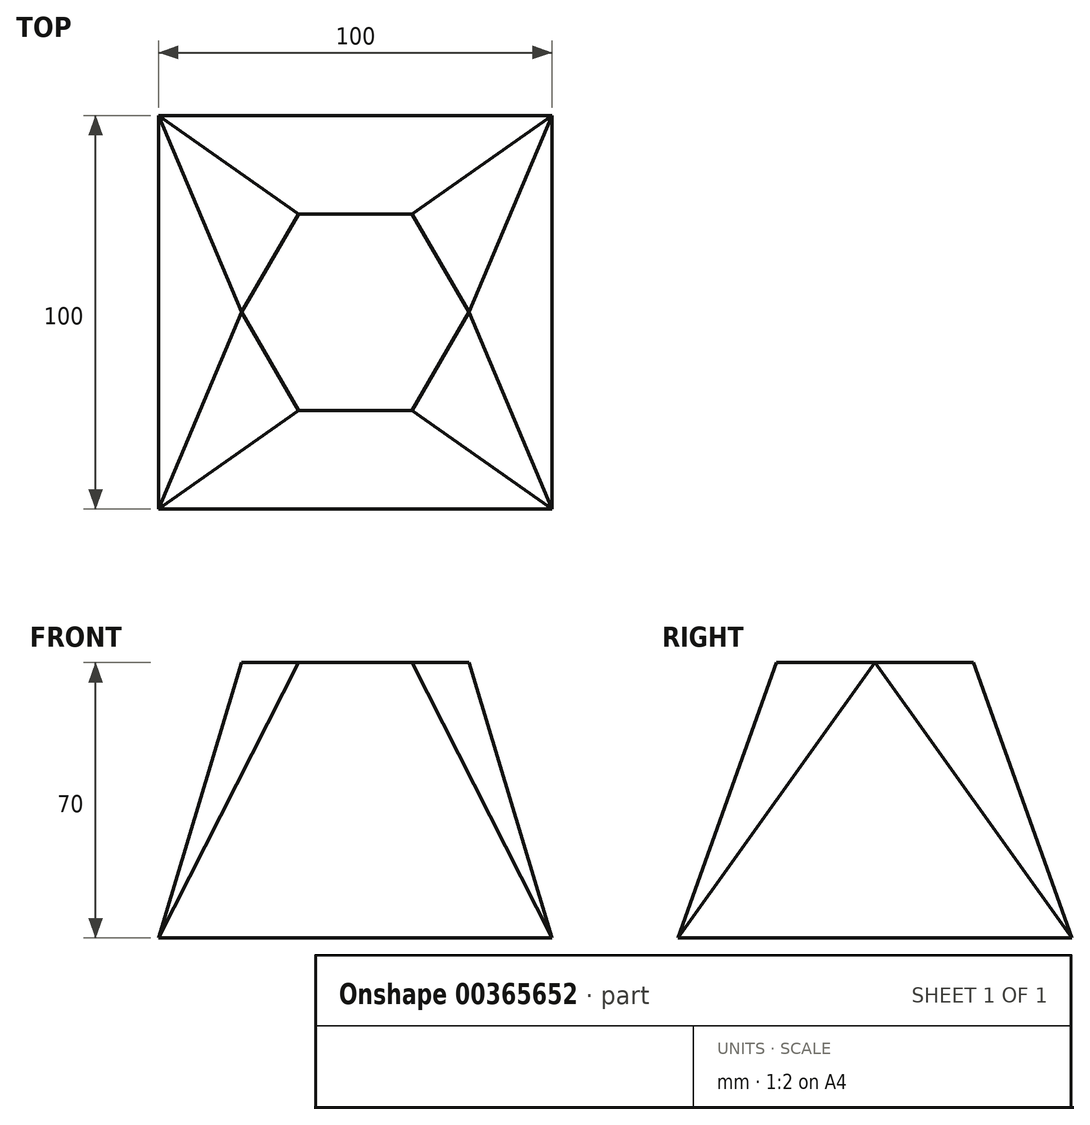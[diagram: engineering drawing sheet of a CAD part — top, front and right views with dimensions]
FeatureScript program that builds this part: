
annotation { "Feature Type Name" : "Feature", "Feature Type Description" : "" }
export const myFeature = defineFeature(function(context is Context, id is Id, definition is map)
    precondition{}
    {
        {
            var Q0;
            Q0=qCreatedBy(makeId("Top.planeOp"),FACE);
            cPlane(context, id + "F0", {"entities" : qUnion([Q0]), "cplaneType" : CPlaneType.OFFSET, "offset" : 70 * mm, "width" : 150 * mm, "height" : 150 * mm});
        }
        {
            var Q0;
            Q0=qCreatedBy(makeId("Top.planeOp"),FACE);
            var sketch = newSketch(context, id + "F1", { "sketchPlane" : qUnion([Q0])});
            skLineSegment(sketch, "E0.bottom", {"start": v(-50, -50) * mm, "end": v(50, -50) * mm});
            skLineSegment(sketch, "E0.top", {"start": v(-50, 50) * mm, "end": v(50, 50) * mm});
            skLineSegment(sketch, "E0.left", {"start": v(-50, -50) * mm, "end": v(-50, 50) * mm});
            skLineSegment(sketch, "E0.right", {"start": v(50, -50) * mm, "end": v(50, 50) * mm});
            skPoint(sketch, "E0.middle", {"position": v(0, 0) * mm});
            skSolve(sketch);
        }
        {
            var Q0;
            Q0=qCreatedBy(id+"F0.planeOp",FACE);
            var sketch = newSketch(context, id + "F2", { "sketchPlane" : qUnion([Q0])});
            skCircle(sketch, "E1.cCircle", {"center": v(0, 0) * mm, "radius": 25 * mm, "construction": true});
            skLineSegment(sketch, "E1.0", {"start": v(-14.43, 25) * mm, "end": v(14.43, 25) * mm});
            skLineSegment(sketch, "E1.1", {"start": v(14.43, 25) * mm, "end": v(28.87, 0) * mm});
            skLineSegment(sketch, "E1.2", {"start": v(28.87, 0) * mm, "end": v(14.43, -25) * mm});
            skLineSegment(sketch, "E1.3", {"start": v(14.43, -25) * mm, "end": v(-14.43, -25) * mm});
            skLineSegment(sketch, "E1.4", {"start": v(-14.43, -25) * mm, "end": v(-28.87, 0) * mm});
            skLineSegment(sketch, "E1.5", {"start": v(-28.87, 0) * mm, "end": v(-14.43, 25) * mm});
            skPoint(sketch, "E1.0.midPoint", {"position": v(0, 25) * mm});
            skLineSegment(sketch, "E2", {"start": v(14.43, 25) * mm, "end": v(28.87, 25) * mm});
            skLineSegment(sketch, "E3", {"start": v(28.87, 25) * mm, "end": v(28.87, 0) * mm});
            skLineSegment(sketch, "E4", {"start": v(28.87, 0) * mm, "end": v(28.87, -25) * mm});
            skLineSegment(sketch, "E5", {"start": v(28.87, -25) * mm, "end": v(14.43, -25) * mm});
            skLineSegment(sketch, "E6", {"start": v(-14.43, -25) * mm, "end": v(-28.87, -25) * mm});
            skLineSegment(sketch, "E7", {"start": v(-28.87, -25) * mm, "end": v(-28.87, 0) * mm});
            skLineSegment(sketch, "E8", {"start": v(-14.43, 25) * mm, "end": v(-28.87, 25) * mm});
            skLineSegment(sketch, "E9", {"start": v(-28.87, 25) * mm, "end": v(-28.87, 0) * mm});
            skSolve(sketch);
        }
        {
            var Q0;
            Q0=qCreatedBy(id+"F0.planeOp",FACE);
            var sketch = newSketch(context, id + "F3", { "sketchPlane" : qUnion([Q0])});
            skLineSegment(sketch, "E10.bottom", {"start": v(28.87, 25) * mm, "end": v(-28.87, 25) * mm});
            skLineSegment(sketch, "E10.top", {"start": v(28.87, -25) * mm, "end": v(-28.87, -25) * mm});
            skLineSegment(sketch, "E10.left", {"start": v(28.87, 25) * mm, "end": v(28.87, -25) * mm});
            skLineSegment(sketch, "E10.right", {"start": v(-28.87, 25) * mm, "end": v(-28.87, -25) * mm});
            skPoint(sketch, "E10.middle", {"position": v(0, 0) * mm});
            skSolve(sketch);
        }
        {
            var Q0;
            Q0=makeQuery(id+"F1.imprint","IMPRINT",FACE,{"disambiguationData":[TD([[makeQuery(id+"F1.imprint","IMPRINT",EDGE,{"derivedFrom":sQuery(id+"F1.wireOp",EDGE,"E0.bottom")}),1.0]])]});
            var Q1;
            Q1 = qSketchRegion(id + "F3", true);
            loft(context, id + "F4", {"sheetProfilesArray" : [{ "sheetProfileEntities" : qUnion([Q0]) }, { "sheetProfileEntities" : qUnion([Q1]) }]});
        }
        {
            var Q1;
            Q1=makeQuery(id+"F2.imprint","IMPRINT",FACE,{"disambiguationData":[TD([[makeQuery(id+"F2.imprint","IMPRINT",EDGE,{"derivedFrom":sQuery(id+"F2.wireOp",EDGE,"E1.5")}),1.0]])]});
            var Q2;
            Q2=makeQuery(id+"F4.opLoft","MID_CAP_VERTEX",VERTEX,{"disambiguationData":[OSD([sQuery(id+"F1.wireOp",EDGE,"E0.top"),sQuery(id+"F1.wireOp",EDGE,"E0.left")])],"capPos":0.0});
            loft(context, id + "F5", {"operationType" : NewBodyOperationType.REMOVE, "sheetProfilesArray" : [{ "sheetProfileEntities" : qUnion([Q1]) }, { "sheetProfileEntities" : qUnion([Q2]) }]});
        }
        {
            var Q1;
            Q1=makeQuery(id+"F2.imprint","IMPRINT",FACE,{"disambiguationData":[TD([[makeQuery(id+"F2.imprint","IMPRINT",EDGE,{"derivedFrom":sQuery(id+"F2.wireOp",EDGE,"E1.4")}),1.0]])]});
            var Q2;
            Q2=makeQuery(id+"F4.opLoft","MID_CAP_VERTEX",VERTEX,{"disambiguationData":[OSD([sQuery(id+"F1.wireOp",EDGE,"E0.bottom"),sQuery(id+"F1.wireOp",EDGE,"E0.left")])],"capPos":0.0});
            loft(context, id + "F6", {"operationType" : NewBodyOperationType.REMOVE, "sheetProfilesArray" : [{ "sheetProfileEntities" : qUnion([Q1]) }, { "sheetProfileEntities" : qUnion([Q2]) }]});
        }
        {
            var Q1;
            Q1=makeQuery(id+"F2.imprint","IMPRINT",FACE,{"disambiguationData":[TD([[makeQuery(id+"F2.imprint","IMPRINT",EDGE,{"derivedFrom":sQuery(id+"F2.wireOp",EDGE,"E1.2")}),1.0]])]});
            var Q2;
            Q2=makeQuery(id+"F4.opLoft","MID_CAP_VERTEX",VERTEX,{"disambiguationData":[OSD([sQuery(id+"F1.wireOp",EDGE,"E0.bottom"),sQuery(id+"F1.wireOp",EDGE,"E0.right")])],"capPos":0.0});
            loft(context, id + "F7", {"operationType" : NewBodyOperationType.REMOVE, "sheetProfilesArray" : [{ "sheetProfileEntities" : qUnion([Q1]) }, { "sheetProfileEntities" : qUnion([Q2]) }]});
        }
        {
            var Q1;
            Q1=makeQuery(id+"F2.imprint","IMPRINT",FACE,{"disambiguationData":[TD([[makeQuery(id+"F2.imprint","IMPRINT",EDGE,{"derivedFrom":sQuery(id+"F2.wireOp",EDGE,"E1.1")}),1.0]])]});
            var Q2;
            Q2=makeQuery(id+"F4.opLoft","MID_CAP_VERTEX",VERTEX,{"disambiguationData":[OSD([sQuery(id+"F1.wireOp",EDGE,"E0.top"),sQuery(id+"F1.wireOp",EDGE,"E0.right")])],"capPos":0.0});
            loft(context, id + "F8", {"operationType" : NewBodyOperationType.REMOVE, "sheetProfilesArray" : [{ "sheetProfileEntities" : qUnion([Q1]) }, { "sheetProfileEntities" : qUnion([Q2]) }]});
        }
    });
